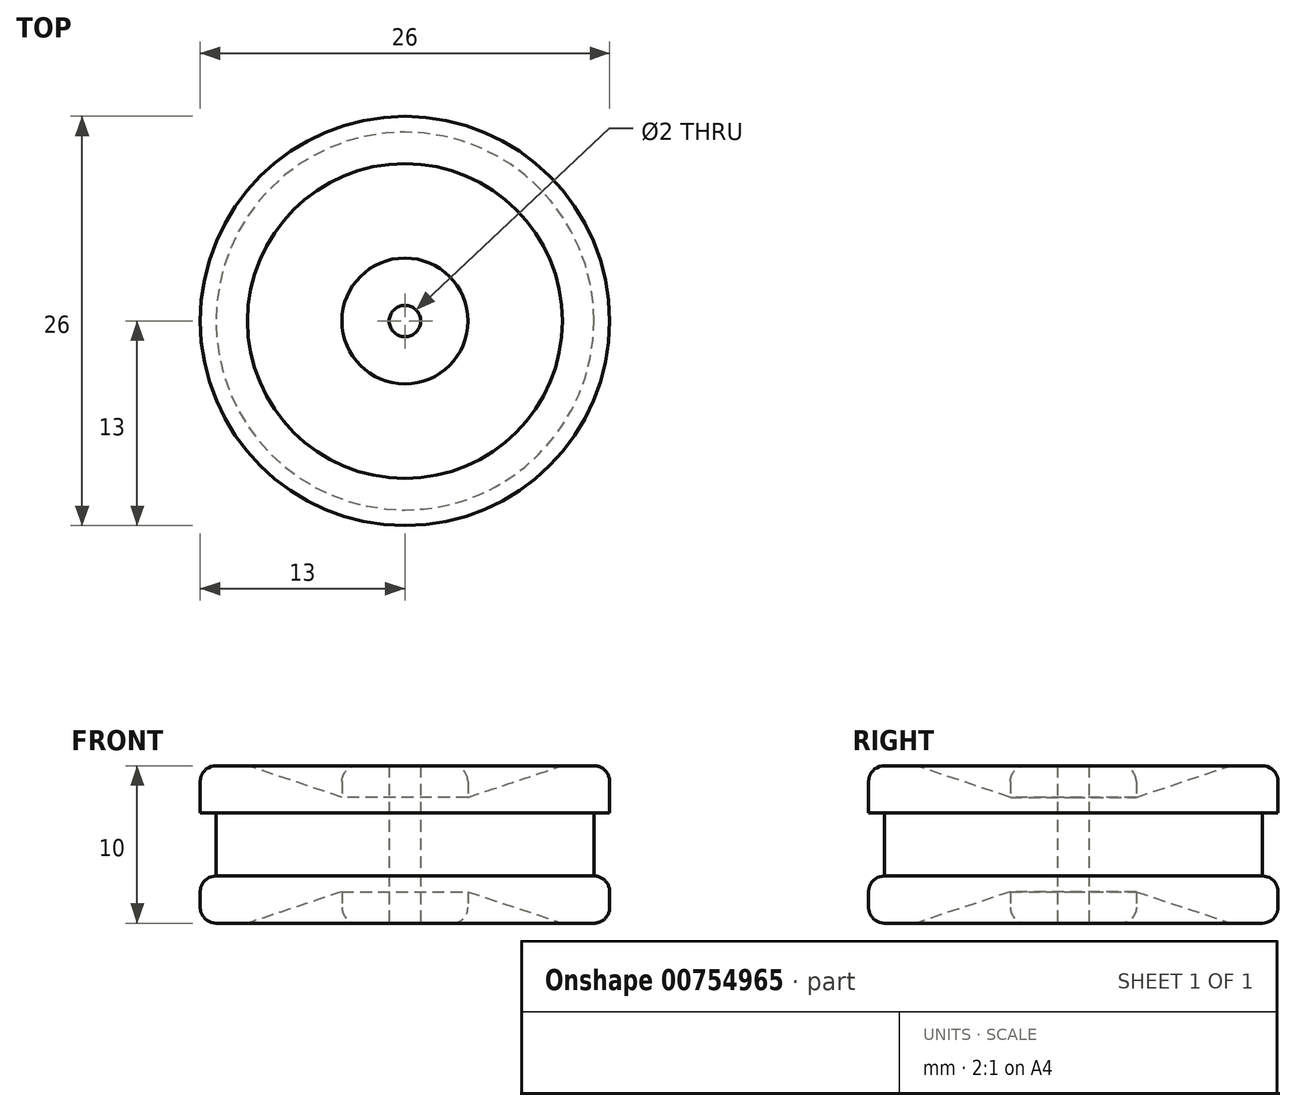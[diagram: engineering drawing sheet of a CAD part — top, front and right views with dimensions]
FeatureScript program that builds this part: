
annotation { "Feature Type Name" : "Feature", "Feature Type Description" : "" }
export const myFeature = defineFeature(function(context is Context, id is Id, definition is map)
    precondition{}
    {
        {
            var Q0;
            Q0=qCreatedBy(makeId("Top.planeOp"),FACE);
            var sketch = newSketch(context, id + "F0", { "sketchPlane" : qUnion([Q0])});
            skCircle(sketch, "E0", {"center": v(0, 0) * mm, "radius": 13 * mm});
            skCircle(sketch, "E1", {"center": v(0, 0) * mm, "radius": 1 * mm});
            skSolve(sketch);
        }
        {
            var Q0;
            Q0=qSketchRegion(id+"F0",true);
            extrude(context, id + "F1", {"entities" : qUnion([Q0]), "depth" : 10 * mm, "offsetDistance" : 25 * mm});
        }
        {
            var Q0;
            Q0=makeQuery(id+"F1.opExtrude","CAP_FACE",FACE,{"disambiguationData":[OSD([sQuery(id+"F0.wireOp",EDGE,"E0"),sQuery(id+"F0.wireOp",EDGE,"E1")])],"isStart":false});
            cPlane(context, id + "F2", {"entities" : qUnion([Q0]), "cplaneType" : CPlaneType.OFFSET, "offset" : 2 * mm, "oppositeDirection" : true, "width" : 150 * mm, "height" : 150 * mm});
        }
        {
            var Q0;
            Q0=qCreatedBy(id+"F2.planeOp",FACE);
            var sketch = newSketch(context, id + "F3", { "sketchPlane" : qUnion([Q0])});
            skCircle(sketch, "E2", {"center": v(0, 0) * mm, "radius": 4 * mm});
            skSolve(sketch);
        }
        {
            var Q0;
            Q0=makeQuery(id+"F1.opExtrude","CAP_FACE",FACE,{"disambiguationData":[OSD([sQuery(id+"F0.wireOp",EDGE,"E0"),sQuery(id+"F0.wireOp",EDGE,"E1")])],"isStart":false});
            var sketch = newSketch(context, id + "F4", { "sketchPlane" : qUnion([Q0])});
            skCircle(sketch, "E3", {"center": v(0, 0) * mm, "radius": 10 * mm});
            skSolve(sketch);
        }
        {
            var Q1;
            Q1=qSketchRegion(id+"F4",true);
            var Q2;
            Q2=qSketchRegion(id+"F3",true);
            loft(context, id + "F5", {"operationType" : NewBodyOperationType.REMOVE, "sheetProfilesArray" : [{ "sheetProfileEntities" : qUnion([Q1]) }, { "sheetProfileEntities" : qUnion([Q2]) }]});
        }
        {
            var Q0;
            Q0=makeQuery(id+"F0.imprint","IMPRINT",FACE,{"disambiguationData":[TD([[makeQuery(id+"F0.imprint","IMPRINT",EDGE,{"derivedFrom":sQuery(id+"F0.wireOp",EDGE,"E0")}),1.0]])]});
            cPlane(context, id + "F6", {"entities" : qUnion([Q0]), "cplaneType" : CPlaneType.OFFSET, "offset" : 2 * mm, "width" : 150 * mm, "height" : 150 * mm});
        }
        {
            var Q0;
            Q0=qCreatedBy(id+"F6.planeOp",FACE);
            var sketch = newSketch(context, id + "F7", { "sketchPlane" : qUnion([Q0])});
            skCircle(sketch, "E4", {"center": v(0, 0) * mm, "radius": 4 * mm});
            skSolve(sketch);
        }
        {
            var Q0;
            Q0=makeQuery(id+"F0.imprint","IMPRINT",FACE,{"disambiguationData":[TD([[makeQuery(id+"F0.imprint","IMPRINT",EDGE,{"derivedFrom":sQuery(id+"F0.wireOp",EDGE,"E0")}),1.0]])]});
            var sketch = newSketch(context, id + "F8", { "sketchPlane" : qUnion([Q0])});
            skCircle(sketch, "E5", {"center": v(0, 0) * mm, "radius": 10 * mm});
            skSolve(sketch);
        }
        {
            var Q1;
            Q1=qSketchRegion(id+"F8",true);
            var Q2;
            Q2=qSketchRegion(id+"F7",true);
            loft(context, id + "F9", {"operationType" : NewBodyOperationType.REMOVE, "sheetProfilesArray" : [{ "sheetProfileEntities" : qUnion([Q1]) }, { "sheetProfileEntities" : qUnion([Q2]) }]});
        }
        {
            var Q0;
            Q0=makeQuery(id+"F5.boolean.opBoolean","COPY",FACE,{"derivedFrom":makeQuery(id+"F5.opLoft","CAP_FACE",FACE,{"disambiguationData":[OSD([makeQuery(id+"F3.imprint","IMPRINT",FACE,{"disambiguationData":[TD([[makeQuery(id+"F3.imprint","IMPRINT",EDGE,{"derivedFrom":sQuery(id+"F3.wireOp",EDGE,"E2")}),1.0]])]})])],"isStart":true})});
            extrude(context, id + "F10", {"entities" : qUnion([Q0]), "operationType" : NewBodyOperationType.ADD, "depth" : 2 * mm, "offsetDistance" : 25 * mm});
        }
        {
            var Q0;
            Q0=makeQuery(id+"F0.imprint","IMPRINT",FACE,{"disambiguationData":[TD([[makeQuery(id+"F0.imprint","IMPRINT",EDGE,{"derivedFrom":sQuery(id+"F0.wireOp",EDGE,"E0")}),1.0]])]});
            var sketch = newSketch(context, id + "F11", { "sketchPlane" : qUnion([Q0])});
            skCircle(sketch, "E6", {"center": v(0, 0) * mm, "radius": 4 * mm});
            skCircle(sketch, "E7", {"center": v(0, 0) * mm, "radius": 1 * mm});
            skSolve(sketch);
        }
        {
            var Q0;
            Q0=qSketchRegion(id+"F11",true);
            extrude(context, id + "F12", {"entities" : qUnion([Q0]), "operationType" : NewBodyOperationType.ADD, "endBound" : BoundingType.UP_TO_NEXT, "depth" : 25 * mm, "offsetDistance" : 25 * mm});
        }
        {
            var Q0;
            Q0=qCreatedBy(makeId("Top.planeOp"),FACE);
            cPlane(context, id + "F13", {"entities" : qUnion([Q0]), "cplaneType" : CPlaneType.OFFSET, "offset" : 3 * mm, "width" : 150 * mm, "height" : 150 * mm});
        }
        {
            var Q0;
            Q0=qCreatedBy(id+"F13.planeOp",FACE);
            var sketch = newSketch(context, id + "F14", { "sketchPlane" : qUnion([Q0])});
            skCircle(sketch, "E8", {"center": v(0, 0) * mm, "radius": 13 * mm});
            skCircle(sketch, "E9", {"center": v(0, 0) * mm, "radius": 12 * mm});
            skSolve(sketch);
        }
        {
            var Q0;
            Q0=qSketchRegion(id+"F14",true);
            extrude(context, id + "F15", {"entities" : qUnion([Q0]), "operationType" : NewBodyOperationType.REMOVE, "depth" : 4 * mm, "offsetDistance" : 25 * mm});
        }
        {
            var Q0;
            Q0=makeQuery(id+"F10.opExtrude","CAP_EDGE",EDGE,{"disambiguationData":[OSD([sQuery(id+"F3.wireOp",EDGE,"E2")])],"isStart":false});
            var Q1;
            Q1=makeQuery(id+"F12.opExtrude","CAP_EDGE",EDGE,{"disambiguationData":[OSD([sQuery(id+"F11.wireOp",EDGE,"E6")])],"isStart":true});
            var Q2;
            Q2=makeQuery(id+"F1.opExtrude","CAP_EDGE",EDGE,{"disambiguationData":[OSD([sQuery(id+"F0.wireOp",EDGE,"E0")])],"isStart":false});
            var Q3;
            Q3=makeQuery(id+"F1.opExtrude","CAP_EDGE",EDGE,{"disambiguationData":[OSD([sQuery(id+"F0.wireOp",EDGE,"E0")])],"isStart":true});
            var Q4;
            Q4=makeQuery(id+"F15.boolean.opBoolean","COPY",EDGE,{"derivedFrom":makeQuery(id+"F15.opExtrude","CAP_EDGE",EDGE,{"disambiguationData":[OSD([sQuery(id+"F14.wireOp",EDGE,"E8")])],"isStart":false})});
            var Q5;
            Q5=makeQuery(id+"F15.boolean.opBoolean","COPY",EDGE,{"derivedFrom":makeQuery(id+"F15.opExtrude","CAP_EDGE",EDGE,{"disambiguationData":[OSD([sQuery(id+"F14.wireOp",EDGE,"E8")])],"isStart":true})});
            fillet(context, id + "F16", {"entities" : qUnion([Q0, Q1, Q2, Q3, Q4, Q5]), "radius" : 1 * mm, "tangentPropagation" : true, "allowEdgeOverflow" : false});
        }
    });
